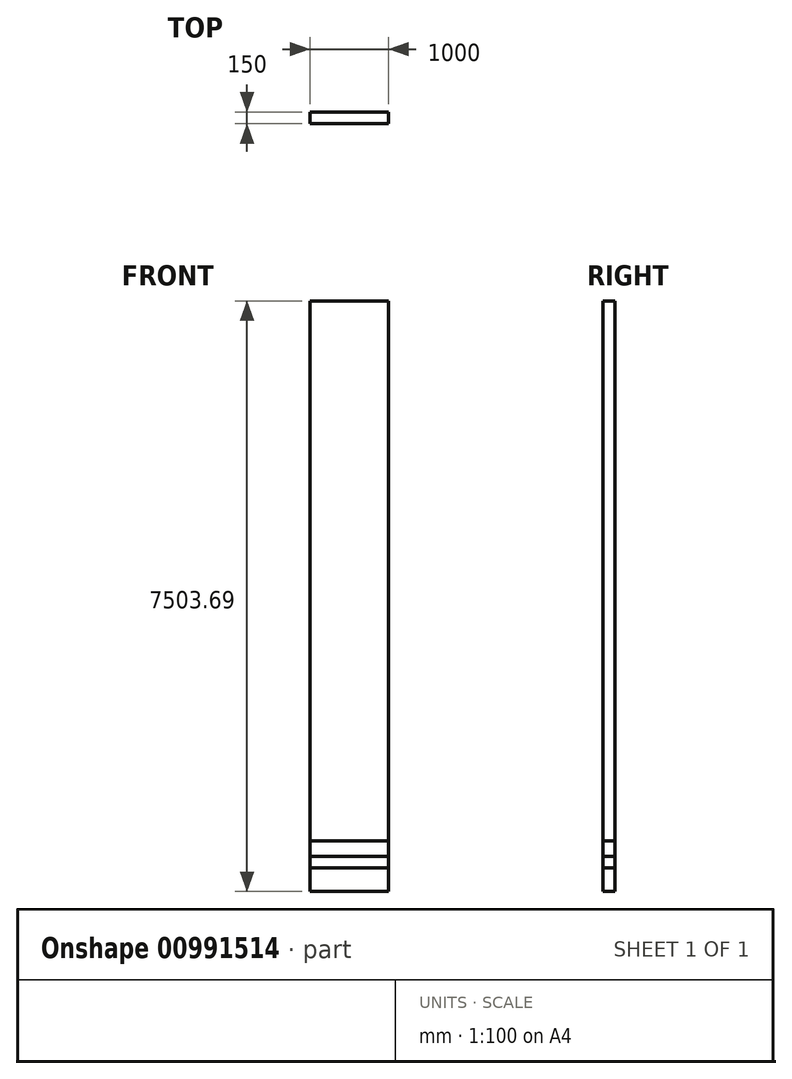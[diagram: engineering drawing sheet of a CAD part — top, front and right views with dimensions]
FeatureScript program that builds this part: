
annotation { "Feature Type Name" : "Feature", "Feature Type Description" : "" }
export const myFeature = defineFeature(function(context is Context, id is Id, definition is map)
    precondition{}
    {
        {
            var Q0;
            Q0=qCreatedBy(makeId("Front.planeOp"),FACE);
            var sketch = newSketch(context, id + "F0", { "sketchPlane" : qUnion([Q0])});
            skLineSegment(sketch, "E0.bottom", {"start": v(500, -150) * mm, "end": v(-500, -150) * mm});
            skLineSegment(sketch, "E0.top", {"start": v(500, 150) * mm, "end": v(-500, 150) * mm});
            skLineSegment(sketch, "E0.left", {"start": v(500, -150) * mm, "end": v(500, 150) * mm});
            skLineSegment(sketch, "E0.right", {"start": v(-500, -150) * mm, "end": v(-500, 150) * mm});
            skPoint(sketch, "E0.middle", {"position": v(0, 0) * mm});
            skSolve(sketch);
        }
        {
            var Q0;
            Q0 = qSketchRegion(id + "F0", true);
            extrude(context, id + "F1", {"entities" : qUnion([Q0]), "endBound" : BoundingType.SYMMETRIC, "depth" : 150 * mm, "offsetDistance" : 25.4 * mm});
        }
        {
            var Q0;
            Q0=qCreatedBy(makeId("Top.planeOp"),FACE);
            cPlane(context, id + "F2", {"entities" : qUnion([Q0]), "cplaneType" : CPlaneType.OFFSET, "offset" : 150 * mm, "width" : 152.4 * mm, "height" : 152.4 * mm});
        }
        {
            var Q0;
            Q0=qCreatedBy(id+"F2.planeOp",FACE);
            var sketch = newSketch(context, id + "F3", { "sketchPlane" : qUnion([Q0])});
            skLineSegment(sketch, "E1.bottom", {"start": v(500, 75) * mm, "end": v(-500, 75) * mm});
            skLineSegment(sketch, "E1.top", {"start": v(500, -75) * mm, "end": v(-500, -75) * mm});
            skLineSegment(sketch, "E1.left", {"start": v(500, 75) * mm, "end": v(500, -75) * mm});
            skLineSegment(sketch, "E1.right", {"start": v(-500, 75) * mm, "end": v(-500, -75) * mm});
            skPoint(sketch, "E1.middle", {"position": v(0, 0) * mm});
            skSolve(sketch);
        }
        {
            var Q0;
            Q0 = qSketchRegion(id + "F3", true);
            extrude(context, id + "F4", {"entities" : qUnion([Q0]), "depth" : 144 * mm, "offsetDistance" : 25.4 * mm});
        }
        {
            var Q0;
            Q0=makeQuery(id+"F4.opExtrude","CAP_FACE",FACE,{"disambiguationData":[OSD([sQuery(id+"F3.wireOp",EDGE,"E1.bottom"),sQuery(id+"F3.wireOp",EDGE,"E1.top"),sQuery(id+"F3.wireOp",EDGE,"E1.left"),sQuery(id+"F3.wireOp",EDGE,"E1.right")])],"isStart":false});
            var sketch = newSketch(context, id + "F5", { "sketchPlane" : qUnion([Q0])});
            skLineSegment(sketch, "E2.bottom", {"start": v(500, -75) * mm, "end": v(-500, -75) * mm});
            skLineSegment(sketch, "E2.top", {"start": v(500, 75) * mm, "end": v(-500, 75) * mm});
            skLineSegment(sketch, "E2.left", {"start": v(500, -75) * mm, "end": v(500, 75) * mm});
            skLineSegment(sketch, "E2.right", {"start": v(-500, -75) * mm, "end": v(-500, 75) * mm});
            skPoint(sketch, "E2.middle", {"position": v(0, 0) * mm});
            skSolve(sketch);
        }
        {
            var Q0;
            Q0=makeQuery(id+"F5.imprint","IMPRINT",FACE,{"disambiguationData":[TD([[makeQuery(id+"F5.imprint","IMPRINT",EDGE,{"derivedFrom":sQuery(id+"F5.wireOp",EDGE,"E2.bottom")}),-1.0]])]});
            extrude(context, id + "F6", {"entities" : qUnion([Q0]), "depth" : 199.9 * mm, "offsetDistance" : 25.4 * mm});
        }
        {
            var Q0;
            Q0=makeQuery(id+"F6.opExtrude","CAP_FACE",FACE,{"disambiguationData":[OSD([sQuery(id+"F5.wireOp",EDGE,"E2.bottom"),sQuery(id+"F5.wireOp",EDGE,"E2.top"),sQuery(id+"F5.wireOp",EDGE,"E2.left"),sQuery(id+"F5.wireOp",EDGE,"E2.right")])],"isStart":false});
            var sketch = newSketch(context, id + "F7", { "sketchPlane" : qUnion([Q0])});
            skLineSegment(sketch, "E3.bottom", {"start": v(500, -75) * mm, "end": v(-500, -75) * mm});
            skLineSegment(sketch, "E3.top", {"start": v(500, 75) * mm, "end": v(-500, 75) * mm});
            skLineSegment(sketch, "E3.left", {"start": v(500, -75) * mm, "end": v(500, 75) * mm});
            skLineSegment(sketch, "E3.right", {"start": v(-500, -75) * mm, "end": v(-500, 75) * mm});
            skPoint(sketch, "E3.middle", {"position": v(0, 0) * mm});
            skSolve(sketch);
        }
        {
            var Q0;
            Q0 = qSketchRegion(id + "F7", true);
            extrude(context, id + "F8", {"entities" : qUnion([Q0]), "depth" : 6859.78 * mm, "offsetDistance" : 25.4 * mm});
        }
    });
